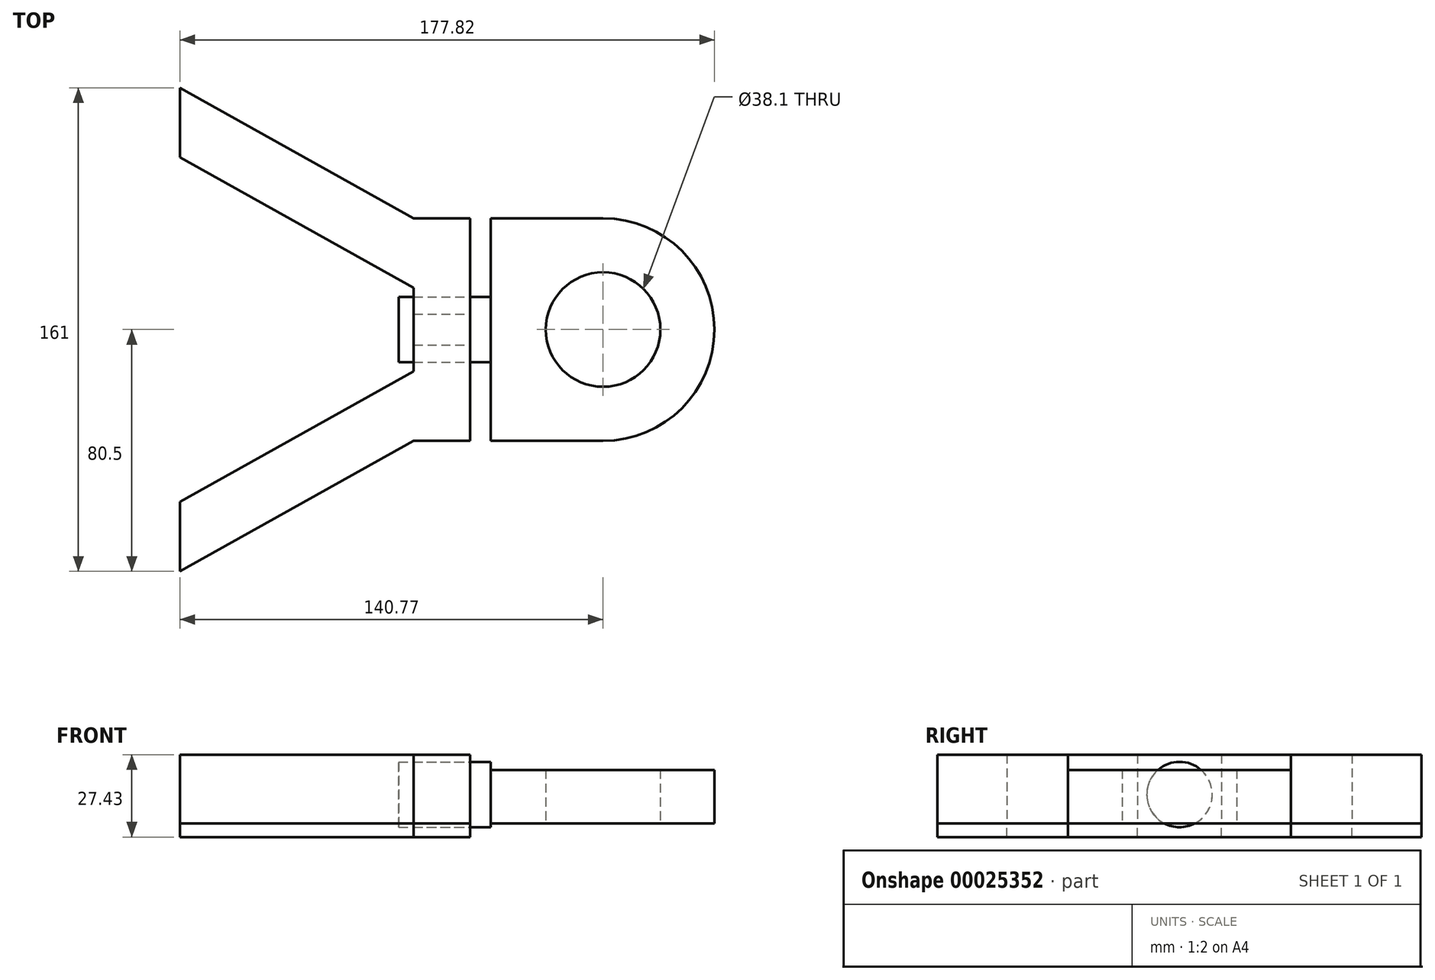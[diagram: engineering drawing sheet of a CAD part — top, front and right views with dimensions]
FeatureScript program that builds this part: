
annotation { "Feature Type Name" : "Feature", "Feature Type Description" : "" }
export const myFeature = defineFeature(function(context is Context, id is Id, definition is map)
    precondition{}
    {
        {
            var Q0;
            Q0=qCreatedBy(makeId("Top.planeOp"),FACE);
            var sketch = newSketch(context, id + "F0", { "sketchPlane" : qUnion([Q0])});
            skCircle(sketch, "E0", {"center": v(0, 0) * mm, "radius": 37.05 * mm});
            skCircle(sketch, "E1", {"center": v(0, 0) * mm, "radius": 19.05 * mm});
            skLineSegment(sketch, "E2", {"start": v(0, 37.05) * mm, "end": v(-37.43, 37.05) * mm});
            skLineSegment(sketch, "E3", {"start": v(0, -37.05) * mm, "end": v(-37.43, -37.05) * mm});
            skLineSegment(sketch, "E4", {"start": v(-37.43, -37.05) * mm, "end": v(-37.43, 37.05) * mm});
            skSolve(sketch);
        }
        {
            var Q0;
            Q0 = qSketchRegion(id + "F0", true);
            extrude(context, id + "F1", {"entities" : qUnion([Q0]), "depth" : 17.78 * mm});
        }
        {
            var Q0;
            Q0=makeQuery(id+"F1.opExtrude","SWEPT_FACE",FACE,{"disambiguationData":[OSD([sQuery(id+"F0.wireOp",EDGE,"E4")])]});
            var sketch = newSketch(context, id + "F2", { "sketchPlane" : qUnion([Q0])});
            skCircle(sketch, "E5", {"center": v(0, 9.58) * mm, "radius": 10.88 * mm});
            skSolve(sketch);
        }
        {
            var Q0;
            Q0 = qSketchRegion(id + "F2", true);
            extrude(context, id + "F3", {"entities" : qUnion([Q0]), "operationType" : NewBodyOperationType.ADD, "depth" : 30.48 * mm});
        }
        {
            var Q0;
            Q0=qCreatedBy(makeId("Top.planeOp"),FACE);
            var sketch = newSketch(context, id + "F4", { "sketchPlane" : qUnion([Q0])});
            skPoint(sketch, "E6", {"position": v(-37.65, 37.06) * mm});
            skPoint(sketch, "E7", {"position": v(-37.54, -37.07) * mm});
            skLineSegment(sketch, "E8", {"start": v(-44.28, 37.06) * mm, "end": v(-44.28, -37.07) * mm});
            skPoint(sketch, "E9", {"position": v(-62.98, 0) * mm});
            skLineSegment(sketch, "E10", {"start": v(-44.28, -37.07) * mm, "end": v(-62.98, -37.07) * mm});
            skLineSegment(sketch, "E11", {"start": v(-62.98, -37.07) * mm, "end": v(-62.98, 37.06) * mm});
            skLineSegment(sketch, "E12", {"start": v(-62.98, 37.06) * mm, "end": v(-44.28, 37.06) * mm});
            skLineSegment(sketch, "E13", {"start": v(-114.48, 0) * mm, "end": v(0, 0) * mm, "construction": true});
            skLineSegment(sketch, "E14", {"start": v(-62.98, 37.06) * mm, "end": v(-140.77, 80.5) * mm});
            skLineSegment(sketch, "E15", {"start": v(-140.77, 80.5) * mm, "end": v(-140.77, 57.4) * mm});
            skLineSegment(sketch, "E16", {"start": v(-140.77, 57.4) * mm, "end": v(-62.98, 13.95) * mm});
            skLineSegment(sketch, "E17.MirrorCS", {"start": v(-140.77, -80.5) * mm, "end": v(-140.77, -57.4) * mm});
            skLineSegment(sketch, "E18.MirrorCS", {"start": v(-62.98, -37.06) * mm, "end": v(-140.77, -80.5) * mm});
            skLineSegment(sketch, "E19.MirrorCS", {"start": v(-140.77, -57.4) * mm, "end": v(-62.98, -13.95) * mm});
            skSolve(sketch);
        }
        {
            var Q0;
            Q0=makeQuery(id+"F4.imprint","IMPRINT",FACE,{"disambiguationData":[TD([[makeQuery(id+"F4.imprint","IMPRINT",EDGE,{"derivedFrom":sQuery(id+"F4.wireOp",EDGE,"E17.MirrorCS")}),-1.0]])]});
            var Q1;
            Q1=makeQuery(id+"F4.imprint","IMPRINT",FACE,{"disambiguationData":[TD([[makeQuery(id+"F4.imprint","IMPRINT",EDGE,{"derivedFrom":sQuery(id+"F4.wireOp",EDGE,"E8")}),-1.0]])]});
            var Q2;
            {var subQ1=sQuery(id+"F4.wireOp",EDGE,"E14");Q2=makeQuery(id+"F4.imprint","IMPRINT",FACE,{"disambiguationData":[TD([[makeQuery(id+"F4.imprint","IMPRINT",EDGE,{"derivedFrom":subQ1}),1.0]])]});}
            extrude(context, id + "F5", {"entities" : qUnion([Q0, Q1, Q2]), "depth" : 22.86 * mm});
        }
        {
            var Q0;
            Q0 = qSketchRegion(id + "F4", true);
            extrude(context, id + "F6", {"entities" : qUnion([Q0]), "oppositeDirection" : true, "depth" : 4.57 * mm});
        }
        {
            var Q0;
            Q0=sQuery(id+"F2.wireOp",VERTEX,"E5.center");
            var Q1;
            Q1=makeQuery(id+"F5.opExtrude","SWEPT_BODY",BODY,{"disambiguationData":[OSD([sQuery(id+"F4.wireOp",EDGE,"E8"),sQuery(id+"F4.wireOp",EDGE,"E10"),sQuery(id+"F4.wireOp",EDGE,"E11"),sQuery(id+"F4.wireOp",EDGE,"E12"),sQuery(id+"F4.wireOp",EDGE,"E14"),sQuery(id+"F4.wireOp",EDGE,"E15"),sQuery(id+"F4.wireOp",EDGE,"E16"),sQuery(id+"F4.wireOp",EDGE,"E17.MirrorCS"),sQuery(id+"F4.wireOp",EDGE,"E18.MirrorCS"),sQuery(id+"F4.wireOp",EDGE,"E19.MirrorCS")])]});
            hole(context, id + "F7", {"style" : HoleStyle.SIMPLE, "holeDiameter" : 21.76 * mm, "endStyle" : HoleEndStyle.THROUGH, "oppositeDirection" : true, "locations" : qUnion([Q0]), "scope" : qUnion([Q1])});
        }
        {
            var Q0;
            Q0=sQuery(id+"F2.wireOp",VERTEX,"E5.center");
            var Q1;
            Q1=makeQuery(id+"F6.opExtrude","SWEPT_BODY",BODY,{"disambiguationData":[OSD([sQuery(id+"F4.wireOp",EDGE,"E8"),sQuery(id+"F4.wireOp",EDGE,"E10"),sQuery(id+"F4.wireOp",EDGE,"E11"),sQuery(id+"F4.wireOp",EDGE,"E12"),sQuery(id+"F4.wireOp",EDGE,"E14"),sQuery(id+"F4.wireOp",EDGE,"E15"),sQuery(id+"F4.wireOp",EDGE,"E16"),sQuery(id+"F4.wireOp",EDGE,"E17.MirrorCS"),sQuery(id+"F4.wireOp",EDGE,"E18.MirrorCS"),sQuery(id+"F4.wireOp",EDGE,"E19.MirrorCS")])]});
            hole(context, id + "F8", {"style" : HoleStyle.SIMPLE, "holeDiameter" : 21.76 * mm, "endStyle" : HoleEndStyle.THROUGH, "oppositeDirection" : true, "locations" : qUnion([Q0]), "scope" : qUnion([Q1])});
        }
    });
